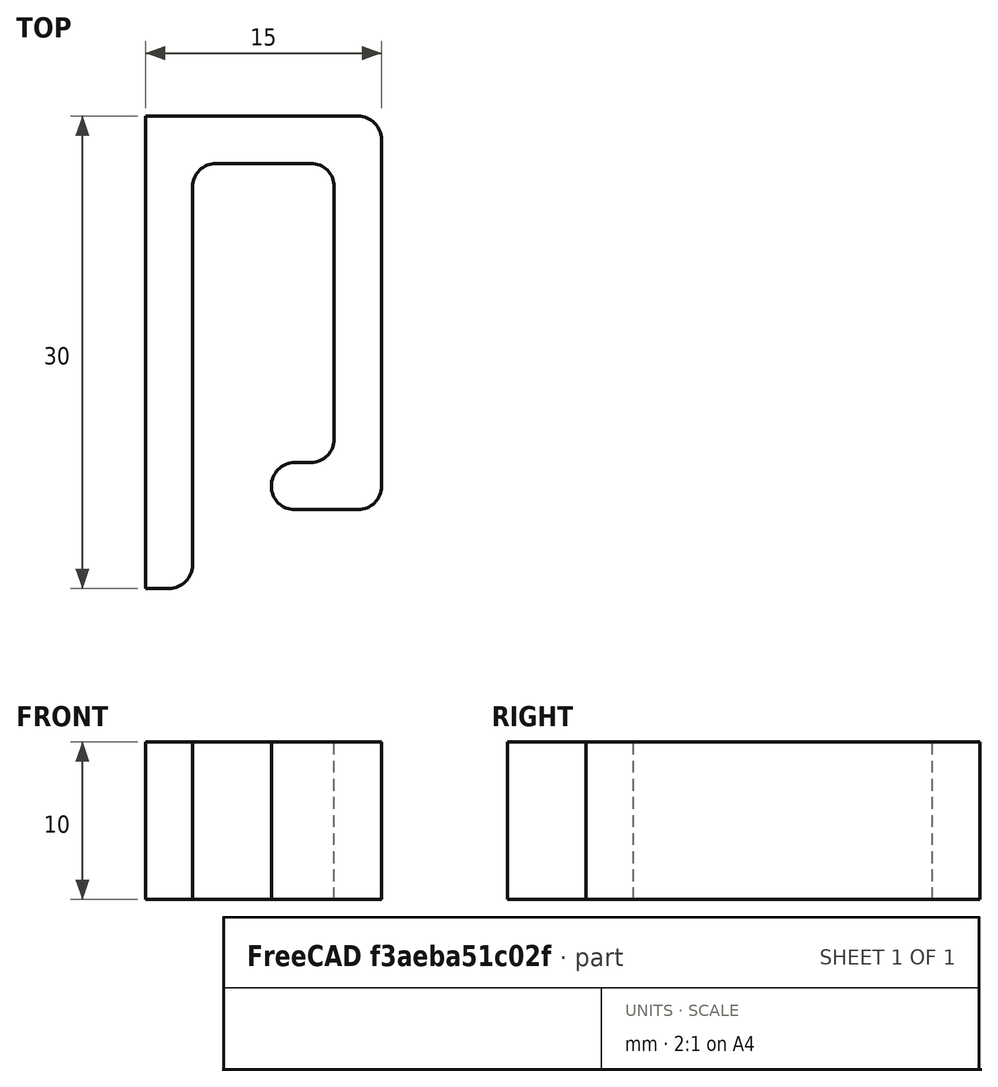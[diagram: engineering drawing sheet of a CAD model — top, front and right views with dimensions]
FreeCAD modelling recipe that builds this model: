
FCSTD DOCUMENT  (FreeCAD 0.21R33771 (Git))
Label: doot
License: All rights reserved
LicenseURL: https://en.wikipedia.org/wiki/All_rights_reserved
objects: Sketcher::SketchObject×1, PartDesign::Pad×1, PartDesign::Body×1
note: 4 computed .brp shape members not serialized (recipe doc carries the construction recipe); baked Part::Feature solids carry a one-line shape summary decoded from their .brp

FEATURE [Sketcher::SketchObject] Sketch
  FullyConstrained = true
  MapMode = 5
  Support = -> [XY_Plane]
  sketch-geometry (39):
    g0: LineSegment StartX=0 StartY=0 StartZ=0 EndX=-3 EndY=0 EndZ=0
    g1: LineSegment StartX=-3 StartY=0 StartZ=0 EndX=-3 EndY=27 EndZ=0
    g2: LineSegment StartX=-3 StartY=27 StartZ=0 EndX=0 EndY=27 EndZ=0
    g3: LineSegment StartX=0 StartY=27 StartZ=0 EndX=0 EndY=0 EndZ=0
    g4: LineSegment StartX=-3 StartY=27 StartZ=0 EndX=12 EndY=27 EndZ=0
    g5: LineSegment StartX=12 StartY=27 StartZ=0 EndX=12 EndY=30 EndZ=0
    g6: LineSegment StartX=12 StartY=30 StartZ=0 EndX=-3 EndY=30 EndZ=0
    g7: LineSegment StartX=-3 StartY=30 StartZ=0 EndX=-3 EndY=27 EndZ=0
    g8: LineSegment StartX=12 StartY=27 StartZ=0 EndX=9 EndY=27 EndZ=0
    g9: LineSegment StartX=9 StartY=27 StartZ=0 EndX=9 EndY=8 EndZ=0
    g10: LineSegment StartX=9 StartY=8 StartZ=0 EndX=12 EndY=8 EndZ=0
    g11: LineSegment StartX=12 StartY=8 StartZ=0 EndX=12 EndY=27 EndZ=0
    g12: LineSegment StartX=12 StartY=8 StartZ=0 EndX=5 EndY=8 EndZ=0
    g13: LineSegment StartX=5 StartY=8 StartZ=0 EndX=5 EndY=5 EndZ=0
    g14: LineSegment StartX=5 StartY=5 StartZ=0 EndX=12 EndY=5 EndZ=0
    g15: LineSegment StartX=12 StartY=5 StartZ=0 EndX=12 EndY=8 EndZ=0
    g16: Circle CenterX=-1.5 CenterY=1.5 CenterZ=0 NormalX=0 NormalY=0 NormalZ=1 AngleXU=0 Radius=1.5
    g17: Circle CenterX=6.5 CenterY=6.5 CenterZ=0 NormalX=0 NormalY=0 NormalZ=1 AngleXU=0 Radius=1.5
    g18: Circle CenterX=10.5 CenterY=6.5 CenterZ=0 NormalX=0 NormalY=0 NormalZ=1 AngleXU=0 Radius=1.5
    g19: Circle CenterX=10.5 CenterY=28.5 CenterZ=0 NormalX=0 NormalY=0 NormalZ=1 AngleXU=0 Radius=1.5
    g20: Circle CenterX=1.5 CenterY=25.5 CenterZ=0 NormalX=0 NormalY=0 NormalZ=1 AngleXU=0 Radius=1.5
    g21: Circle CenterX=7.5 CenterY=25.5 CenterZ=0 NormalX=0 NormalY=0 NormalZ=1 AngleXU=0 Radius=1.5
    g22: Circle CenterX=7.5 CenterY=9.5 CenterZ=0 NormalX=0 NormalY=0 NormalZ=1 AngleXU=0 Radius=1.5
    g23: LineSegment StartX=-3 StartY=30 StartZ=0 EndX=-3 EndY=0 EndZ=0
    g24: LineSegment StartX=-3 StartY=0 StartZ=0 EndX=-1.50001 EndY=2.52314e-11 EndZ=0
    g25: LineSegment StartX=0 StartY=1.5 StartZ=0 EndX=1.02e-14 EndY=25.5 EndZ=0
    g26: LineSegment StartX=1.5 StartY=27 StartZ=0 EndX=7.5 EndY=27 EndZ=0
    g27: LineSegment StartX=9 StartY=25.5 StartZ=0 EndX=9 EndY=9.5 EndZ=0
    g28: LineSegment StartX=6.5 StartY=8 StartZ=0 EndX=7.5 EndY=8 EndZ=0
    g29: LineSegment StartX=6.5 StartY=5 StartZ=0 EndX=10.5 EndY=5 EndZ=0
    g30: LineSegment StartX=12 StartY=6.5 StartZ=0 EndX=12 EndY=28.5 EndZ=0
    g31: LineSegment StartX=-3 StartY=30 StartZ=0 EndX=10.5 EndY=30 EndZ=0
    g32: ArcOfCircle CenterX=10.5 CenterY=28.5 CenterZ=0 NormalX=0 NormalY=0 NormalZ=1 AngleXU=0 Radius=1.5 StartAngle=5.94902e-07 EndAngle=1.5708
    g33: ArcOfCircle CenterX=6.5 CenterY=6.5 CenterZ=0 NormalX=0 NormalY=0 NormalZ=1 AngleXU=0 Radius=1.5 StartAngle=1.5708 EndAngle=4.71239
    g34: ArcOfCircle CenterX=7.5 CenterY=9.5 CenterZ=0 NormalX=0 NormalY=0 NormalZ=1 AngleXU=0 Radius=1.5 StartAngle=4.71239 EndAngle=6.28319
    g35: ArcOfCircle CenterX=10.5 CenterY=6.5 CenterZ=0 NormalX=0 NormalY=0 NormalZ=1 AngleXU=0 Radius=1.5 StartAngle=4.71239 EndAngle=6.28319
    g36: ArcOfCircle CenterX=1.5 CenterY=25.5 CenterZ=0 NormalX=0 NormalY=0 NormalZ=1 AngleXU=0 Radius=1.5 StartAngle=1.5708 EndAngle=3.14159
    g37: ArcOfCircle CenterX=7.5 CenterY=25.5 CenterZ=0 NormalX=0 NormalY=0 NormalZ=1 AngleXU=0 Radius=1.5 StartAngle=6.25877e-08 EndAngle=1.5708
    g38: ArcOfCircle CenterX=-1.5 CenterY=1.5 CenterZ=0 NormalX=0 NormalY=0 NormalZ=1 AngleXU=0 Radius=1.5 StartAngle=4.71238 EndAngle=6.28318
  constraints (112):
    c: Coincident(g0,g1)
    c: Coincident(g1,g2)
    c: Coincident(g2,g3)
    c: Coincident(g3,g0)
    c: Horizontal(g0)
    c: Horizontal(g2)
    c: Vertical(g1)
    c: Vertical(g3)
    c: Coincident(g0,g-1)
    c: Coincident(g4,g5)
    c: Coincident(g5,g6)
    c: Coincident(g6,g7)
    c: Coincident(g7,g4)
    c: Horizontal(g4)
    c: Horizontal(g6)
    c: Vertical(g5)
    c: Vertical(g7)
    c: Coincident(g4,g1)
    c: Coincident(g8,g9)
    c: Coincident(g9,g10)
    c: Coincident(g10,g11)
    c: Coincident(g11,g8)
    c: Horizontal(g8)
    c: Horizontal(g10)
    c: Vertical(g9)
    c: Vertical(g11)
    c: Coincident(g8,g4)
    c: Coincident(g12,g13)
    c: Coincident(g13,g14)
    c: Coincident(g14,g15)
    c: Coincident(g15,g12)
    c: Horizontal(g12)
    c: Horizontal(g14)
    c: Vertical(g13)
    c: Vertical(g15)
    c: Coincident(g12,g10)
    c: Equal(g0,g10)
    c: Equal(g7,g0)
    c: DistanceY(g0,g6) = 30
    c: DistanceX(g0,g0) = 3
    c: DistanceY(g13,g13) = 3
    c: DistanceX(g14,g14) = 7
    c: DistanceX(g6,g6) = 15
    c: DistanceY(g14,g5) = 25
    c: Tangent(g16,g3)
    c: Tangent(g16,g1)
    c: Tangent(g16,g0)
    c: Tangent(g17,g12)
    c: Tangent(g17,g13)
    c: Tangent(g17,g14)
    c: Tangent(g18,g15)
    c: Tangent(g18,g14)
    c: Tangent(g10,g18)
    c: Tangent(g22,g9)
    c: Tangent(g22,g12)
    c: Tangent(g3,g20)
    c: Tangent(g4,g20)
    c: Tangent(g21,g4)
    c: Tangent(g21,g9)
    c: Tangent(g19,g6)
    c: Tangent(g19,g5)
    c: Tangent(g19,g4)
    c: Equal(g20,g21)
    c: Equal(g21,g22)
    c: Diameter(g22) = 3
    c: Coincident(g23,g6)
    c: Coincident(g23,g0)
    c: Coincident(g24,g23)
    c: PointOnObject(g24,g0)
    c: PointOnObject(g25,g16)
    c: PointOnObject(g25,g3)
    c: PointOnObject(g26,g20)
    c: PointOnObject(g26,g21)
    c: PointOnObject(g27,g22)
    c: PointOnObject(g28,g17)
    c: PointOnObject(g28,g12)
    c: Horizontal(g28)
    c: PointOnObject(g29,g14)
    c: PointOnObject(g29,g14)
    c: PointOnObject(g30,g15)
    c: PointOnObject(g30,g5)
    c: Horizontal(g26)
    c: Coincident(g31,g23)
    c: PointOnObject(g31,g19)
    c: Coincident(g32,g31)
    c: Coincident(g32,g30)
    c: Coincident(g19,g32)
    c: Coincident(g33,g17)
    c: Coincident(g33,g29)
    c: Coincident(g33,g28)
    c: Coincident(g34,g22)
    c: Coincident(g34,g27)
    c: Coincident(g34,g28)
    c: Coincident(g35,g18)
    c: Coincident(g35,g30)
    c: Coincident(g35,g29)
    c: Coincident(g36,g20)
    c: Coincident(g36,g25)
    c: Coincident(g36,g26)
    c: Coincident(g37,g21)
    c: Coincident(g37,g26)
    c: Coincident(g37,g27)
    c: Coincident(g38,g16)
    c: Coincident(g38,g25)
    c: Coincident(g38,g24)
    c: PointOnObject(g27,g9)
    c: PointOnObject(g26,g4)
    c: PointOnObject(g31,g6)
    c: PointOnObject(g30,g18)
    c: PointOnObject(g27,g9)
    c: PointOnObject(g25,g3)
    c: DistanceX(g0,g13) = 5
FEATURE [PartDesign::Pad] Pad
  Direction = (0,0,1)
  Length = 10
  Length2 = 10
  Profile = -> Sketch
  ReferenceAxis = -> Sketch [N_Axis]
  Type = 0
FEATURE [PartDesign::Body] Body
  Group = -> [Sketch,Pad]
  Origin = -> Origin
  Tip = -> Pad
